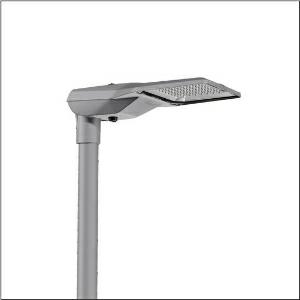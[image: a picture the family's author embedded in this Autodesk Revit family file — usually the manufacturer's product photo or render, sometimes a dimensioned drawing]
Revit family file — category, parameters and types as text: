
# Revit family: streetlight_sl_21_iq_midi___st1_0a_5xe3d31y08mb_3ca9
name_source: partatom
category: Lighting Fixtures
units: mm (PartAtom-declared; Revit-internal decimal feet)

## family parameters
Cut with Voids When Loaded = No
Host = Face
Light Source = No
Part Type = Normal
Room Calculation Point = No
Round Connector Dimension = Use Diameter
Shared = No

## types (1)
- --- (1 x LED, 18340 lm, 129.3 W, 3000K)
    Apparent Load = 129 VA
    CIE Flux Codes = 37 72 97 100 100
    Color Rendering = 70
    Color Temperature = 3000K
    Default Elevation = 1800 mm
    Description = Streetlight SL 21 iQ midi, mast luminaire, primary light control with lens, of PMMA, primary optical cover: cover, of toughened safety glass, transparent, light distribution: ST1.0a, light emission: direct distribution, primary light characteristic: asymmetric, installation type: post-top, side-entry, LED, High Power LED, rated luminous flux: 18.340lm, luminous efficacy: 142lm/W, light colour: 730, colour temperature: 3000K, control gear: iQ-Street Remote, D4i with power reduction, control: pre-setting: logarithmic dimming characteristic, Street-Remote, Auto-Match, Temp-Guard, Lumen-Switch, Night-Set, Smart-Wire, Light-Fading, Desk-Remote (wireless, voltage-free reading and setting of iQ features in the workshop via application-optimized NFC function/RFID function), optimised constant luminous flux control (CLO 2.0), mains connection: 230..240V, AC, 50/60Hz, start of lifetime: 129W, end of service life: 142W, reduction: 56W, luminaire housing, of diecast aluminium, powder-coated, SITECO metallic grey (DB 702S), corrosivity category C5 high according to DIN EN ISO 12944, please order mast flange separately, inclination adjustable: 0°, 5°, 10°, 15°, sealing non-destructively replaceable, multi-level sealing system, length: 644mm, width: 335mm, height: 110mm, mast flange for spigot size: 42mm (side-entry): 5XC10008XM4, 60/48mm (side-entry/post-top): 5XC10108XM2, 76/60mm (side-entry/post-top): 5XC10108XM1, mounting height: 4..8m, Smart Interface below and above, protection rating (complete): IP66, insulation class (complete): insulation class II (safety insulation), certification: CE, ENEC, ENEC+, VDE, impact resistance: IK10, permissible operating ambient temperature for outdoor applications: -40..+50°C, standard-compliant lighting for roads and squares, packaging unit: 1 piece

Light Distribution: ST1.0a
    Height = 111 mm
    Lamp = 1 x LED
    Lamp Light Flux = 18340 lm
    Lamp Power = 129.3 W
    Lamp count = 1
    Length = 644 mm
    Luminous efficacy = 142 lm/W
    Manufacturer = Siteco
    ModVariant = No
    Model = 5XE3D31Y08MB
    Number of Poles = 1
    OnlyDefault = Yes
    Power Factor = 1
    Product Name = Streetlight SL 21 iQ midi | ST1.0a
    Product group = mast luminaire | pylon top
    ProductGroupID = 6100
    Protection Class = Protection class II
    Protection Degree = IP 66
    RLX_Detail_Level = 1
    RLX_Emergency_Light_Flux = 0 lm
    RLX_Emergency_Type = 0
    RLX_Emergency_Type_DB = No
    RlxData = <blob elided: 91073 chars, md5=6aad5ab8>
    Socket = socket
    Standby Power = 0 W
    System Light Flux = 18340 lm
    System Power = 129 W
    Type Comments = factory setting: luminous flux: 100 % | dim-lin: 254 | 672 mA
    Type Image = l_1004304.jpg
    URL = http://relux.com
    VarID = @adj_114653
    Voltage = 0 V
    Weight = 0.00 kg
    Width = 336 mm

## geometry (parser evidence)
native form markers: Blend x4, Sweep x11
no freeform markers — native parametric forms only
